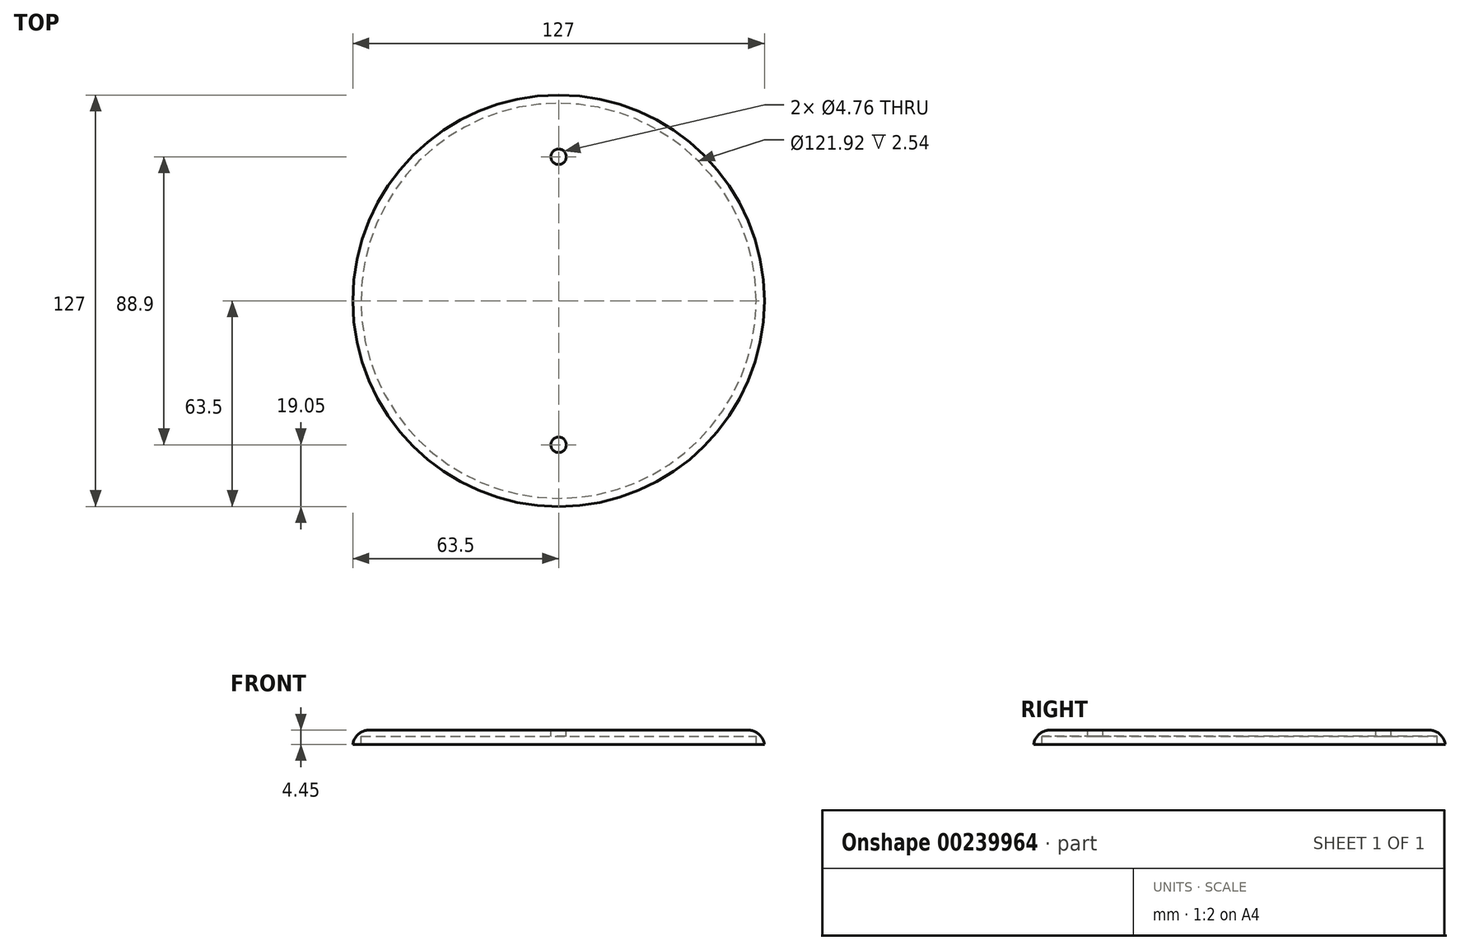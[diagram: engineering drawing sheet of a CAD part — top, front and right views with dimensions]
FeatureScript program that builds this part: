
annotation { "Feature Type Name" : "Feature", "Feature Type Description" : "" }
export const myFeature = defineFeature(function(context is Context, id is Id, definition is map)
    precondition{}
    {
        {
            var Q0;
            Q0=qCreatedBy(makeId("Top.planeOp"),FACE);
            var sketch = newSketch(context, id + "F0", { "sketchPlane" : qUnion([Q0])});
            skCircle(sketch, "E0", {"center": v(0, 0) * mm, "radius": 63.5 * mm});
            skSolve(sketch);
        }
        {
            var Q0;
            Q0 = qSketchRegion(id + "F0", true);
            extrude(context, id + "F1", {"entities" : qUnion([Q0]), "depth" : 1.9 * mm});
        }
        {
            var Q0;
            Q0=makeQuery(id+"F1.opExtrude","CAP_FACE",FACE,{"disambiguationData":[OSD([sQuery(id+"F0.wireOp",EDGE,"E0")])],"isStart":false});
            var sketch = newSketch(context, id + "F2", { "sketchPlane" : qUnion([Q0])});
            skCircle(sketch, "E1", {"center": v(0, 44.45) * mm, "radius": 2.38 * mm});
            skCircle(sketch, "E2", {"center": v(0, -44.45) * mm, "radius": 2.38 * mm});
            skSolve(sketch);
        }
        {
            var Q0;
            Q0 = qSketchRegion(id + "F2", true);
            extrude(context, id + "F3", {"entities" : qUnion([Q0]), "operationType" : NewBodyOperationType.REMOVE, "endBound" : BoundingType.THROUGH_ALL, "oppositeDirection" : true, "depth" : 25.4 * mm});
        }
        {
            var Q0;
            Q0=makeQuery(id+"F1.opExtrude","CAP_FACE",FACE,{"disambiguationData":[OSD([sQuery(id+"F0.wireOp",EDGE,"E0")])],"isStart":true});
            var sketch = newSketch(context, id + "F4", { "sketchPlane" : qUnion([Q0])});
            skCircle(sketch, "E3", {"center": v(0, 0) * mm, "radius": 60.96 * mm});
            skCircle(sketch, "E4", {"center": v(0, 0) * mm, "radius": 63.5 * mm});
            skSolve(sketch);
        }
        {
            var Q0;
            Q0=makeQuery(id+"F4.imprint","IMPRINT",FACE,{"disambiguationData":[TD([[makeQuery(id+"F4.imprint","IMPRINT",EDGE,{"derivedFrom":sQuery(id+"F4.wireOp",EDGE,"E3")}),-1.0]])]});
            extrude(context, id + "F5", {"entities" : qUnion([Q0]), "operationType" : NewBodyOperationType.ADD, "depth" : 2.54 * mm});
        }
        {
            var Q0;
            Q0=makeQuery(id+"F1.opExtrude","CAP_EDGE",EDGE,{"disambiguationData":[OSD([sQuery(id+"F0.wireOp",EDGE,"E0")])],"isStart":false});
            fillet(context, id + "F6", {"entities" : qUnion([Q0]), "radius" : 5.08 * mm, "tangentPropagation" : true, "allowEdgeOverflow" : false});
        }
    });
